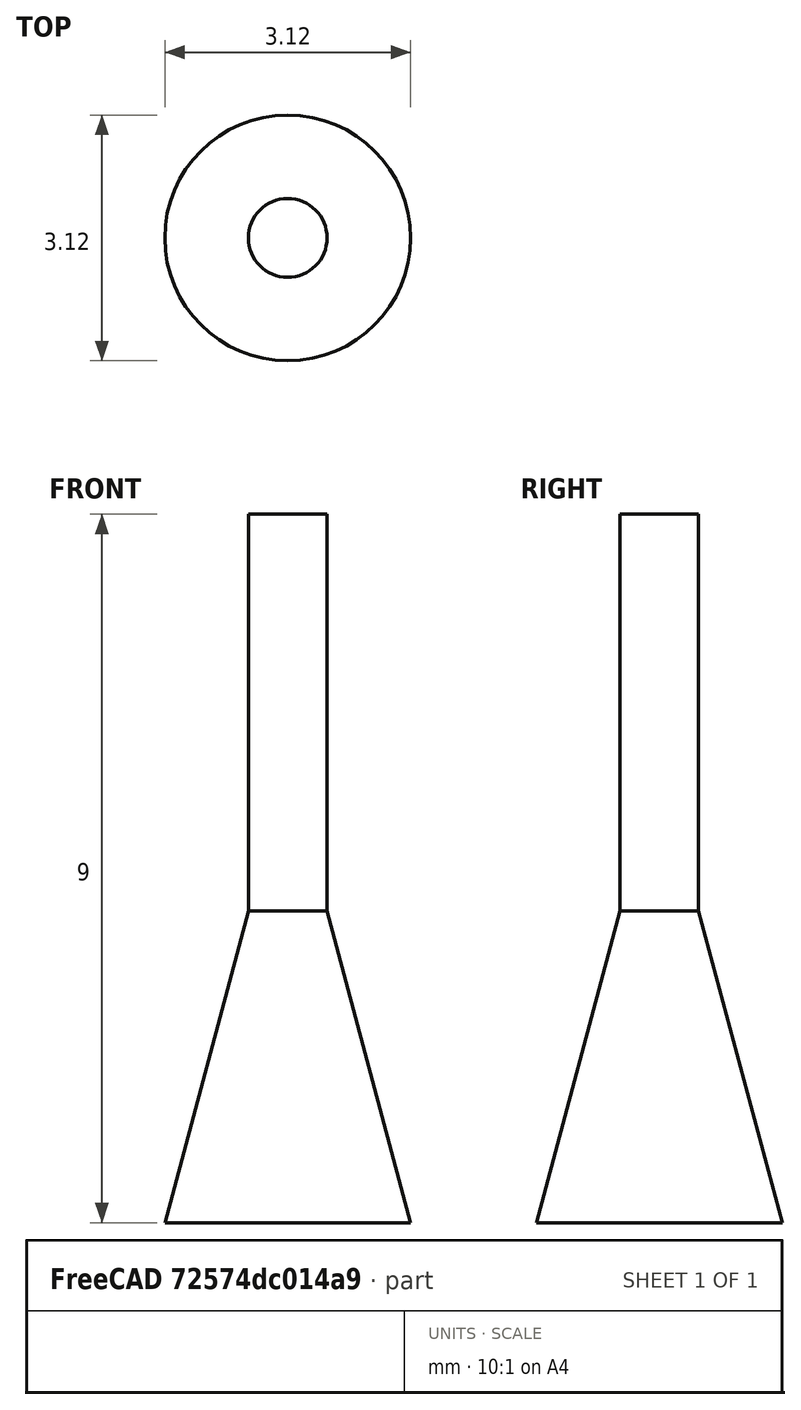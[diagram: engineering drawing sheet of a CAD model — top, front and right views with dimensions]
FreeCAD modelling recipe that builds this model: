
FCSTD DOCUMENT  (FreeCAD 0.20R29177 +233 (Git))
Label: tongue_sucker
License: All rights reserved
LicenseURL: http://en.wikipedia.org/wiki/All_rights_reserved
objects: Sketcher::SketchObject×1, PartDesign::Revolution×1, PartDesign::Body×1
note: 4 computed .brp shape members not serialized (recipe doc carries the construction recipe); baked Part::Feature solids carry a one-line shape summary decoded from their .brp

FEATURE [Sketcher::SketchObject] Sketch
  FullyConstrained = false
  MapMode = 5
  Placement = pos=(0,0,0) rot=(1,0,0;1.5708rad)
  Support = -> [XZ_Plane]
  sketch-geometry (5):
    g0: LineSegment StartX=0.5 StartY=3.9603 StartZ=0 EndX=1.56116 EndY=0 EndZ=0
    g1: LineSegment StartX=0.5 StartY=3.9603 StartZ=0 EndX=0.5 EndY=9.0003 EndZ=0
    g2: LineSegment StartX=0.5 StartY=9.0003 StartZ=0 EndX=0 EndY=9.0003 EndZ=0
    g3: LineSegment StartX=0 StartY=9.0003 StartZ=0 EndX=0 EndY=0 EndZ=0
    g4: LineSegment StartX=0 StartY=0 StartZ=0 EndX=1.56116 EndY=0 EndZ=0
  constraints (14):
    c: Distance(g0) = 4.1
    c: Angle(g-2,g0) = 0.261799
    c: PointOnObject(g0,g-1)
    c: Distance(g0,g-2) = 0.5
    c: Coincident(g1,g0)
    c: Vertical(g1)
    c: DistanceY(g1,g1) = 5.04
    c: Coincident(g2,g1)
    c: PointOnObject(g2,g-2)
    c: Horizontal(g2)
    c: Coincident(g3,g2)
    c: Coincident(g4,g3)
    c: Coincident(g4,g0)
    c: Horizontal(g4)
FEATURE [PartDesign::Revolution] Revolution
  Angle = 360
  Axis = (0,2e-16,1)
  Base = (0,0,0)
  Placement = pos=(0,0,0) rot=(1,0,0;1.5708rad)
  Profile = -> Sketch
  ReferenceAxis = -> Sketch [V_Axis]
  Reversed = true
FEATURE [PartDesign::Body] Body
  Group = -> [Sketch,Revolution]
  Origin = -> Origin
  Tip = -> Revolution
